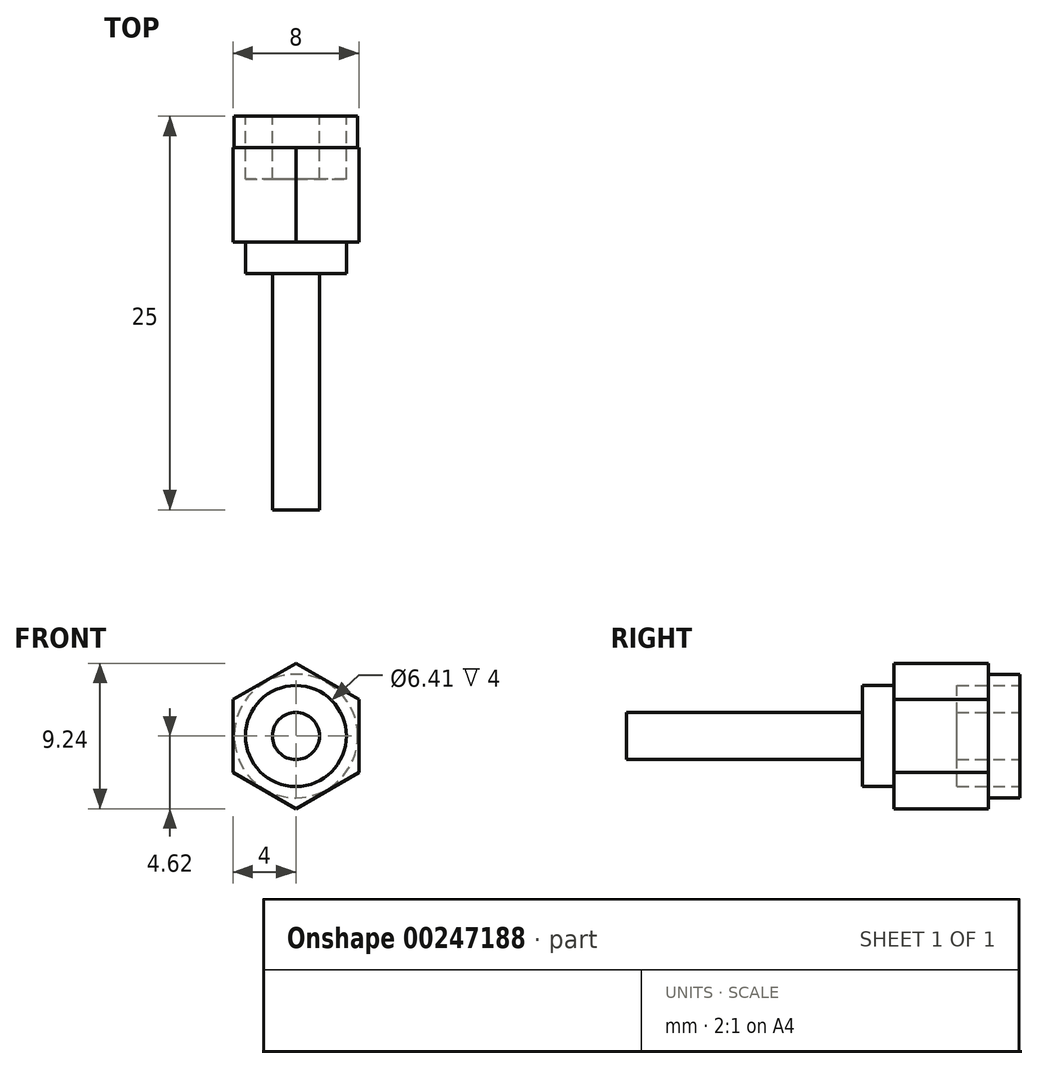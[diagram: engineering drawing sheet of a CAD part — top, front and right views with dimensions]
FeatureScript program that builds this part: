
annotation { "Feature Type Name" : "Feature", "Feature Type Description" : "" }
export const myFeature = defineFeature(function(context is Context, id is Id, definition is map)
    precondition{}
    {
        {
            var Q0;
            Q0=qCreatedBy(makeId("Front.planeOp"),FACE);
            var sketch = newSketch(context, id + "F0", { "sketchPlane" : qUnion([Q0])});
            skCircle(sketch, "E0", {"center": v(0, 0) * mm, "radius": 1.5 * mm});
            skCircle(sketch, "E1.cCircle", {"center": v(0, 0) * mm, "radius": 4 * mm, "construction": true});
            skLineSegment(sketch, "E1.0", {"start": v(4, 2.3) * mm, "end": v(4, -2.3) * mm});
            skLineSegment(sketch, "E1.1", {"start": v(4, -2.3) * mm, "end": v(0, -4.62) * mm});
            skLineSegment(sketch, "E1.2", {"start": v(0, -4.62) * mm, "end": v(-4, -2.3) * mm});
            skLineSegment(sketch, "E1.3", {"start": v(-4, -2.3) * mm, "end": v(-4, 2.3) * mm});
            skLineSegment(sketch, "E1.4", {"start": v(-4, 2.3) * mm, "end": v(0, 4.62) * mm});
            skLineSegment(sketch, "E1.5", {"start": v(0, 4.62) * mm, "end": v(4, 2.3) * mm});
            skPoint(sketch, "E1.0.midPoint", {"position": v(4, 0) * mm});
            skCircle(sketch, "E2", {"center": v(0, 0) * mm, "radius": 3.93 * mm});
            skCircle(sketch, "E3", {"center": v(0, 0) * mm, "radius": 3.2 * mm});
            skSolve(sketch);
        }
        {
            var Q0;
            Q0=makeQuery(id+"F0.imprint","IMPRINT",FACE,{"disambiguationData":[TD([[makeQuery(id+"F0.imprint","IMPRINT",EDGE,{"derivedFrom":sQuery(id+"F0.wireOp",EDGE,"E0")}),1.0]])]});
            extrude(context, id + "F1", {"entities" : qUnion([Q0]), "depth" : 25 * mm});
        }
        {
            var Q0;
            Q0=makeQuery(id+"F0.imprint","IMPRINT",FACE,{"disambiguationData":[TD([[makeQuery(id+"F0.imprint","IMPRINT",EDGE,{"derivedFrom":sQuery(id+"F0.wireOp",EDGE,"E1.0")}),-1.0]])]});
            extrude(context, id + "F2", {"entities" : qUnion([Q0]), "depth" : 8 * mm, "hasSecondDirection" : true, "secondDirectionOppositeDirection" : false, "secondDirectionDepth" : 2 * mm});
        }
        {
            var Q0;
            Q0=makeQuery(id+"F0.imprint","IMPRINT",FACE,{"disambiguationData":[TD([[makeQuery(id+"F0.imprint","IMPRINT",EDGE,{"derivedFrom":sQuery(id+"F0.wireOp",EDGE,"E0")}),-1.0]])]});
            extrude(context, id + "F3", {"entities" : qUnion([Q0]), "operationType" : NewBodyOperationType.ADD, "depth" : 10 * mm, "hasSecondDirection" : true, "secondDirectionOppositeDirection" : false, "secondDirectionDepth" : 4 * mm});
        }
        {
            var Q0;
            Q0=makeQuery(id+"F0.imprint","IMPRINT",FACE,{"disambiguationData":[TD([[makeQuery(id+"F0.imprint","IMPRINT",EDGE,{"derivedFrom":sQuery(id+"F0.wireOp",EDGE,"E2")}),1.0]])]});
            extrude(context, id + "F4", {"entities" : qUnion([Q0]), "operationType" : NewBodyOperationType.ADD, "depth" : 8 * mm});
        }
    });
